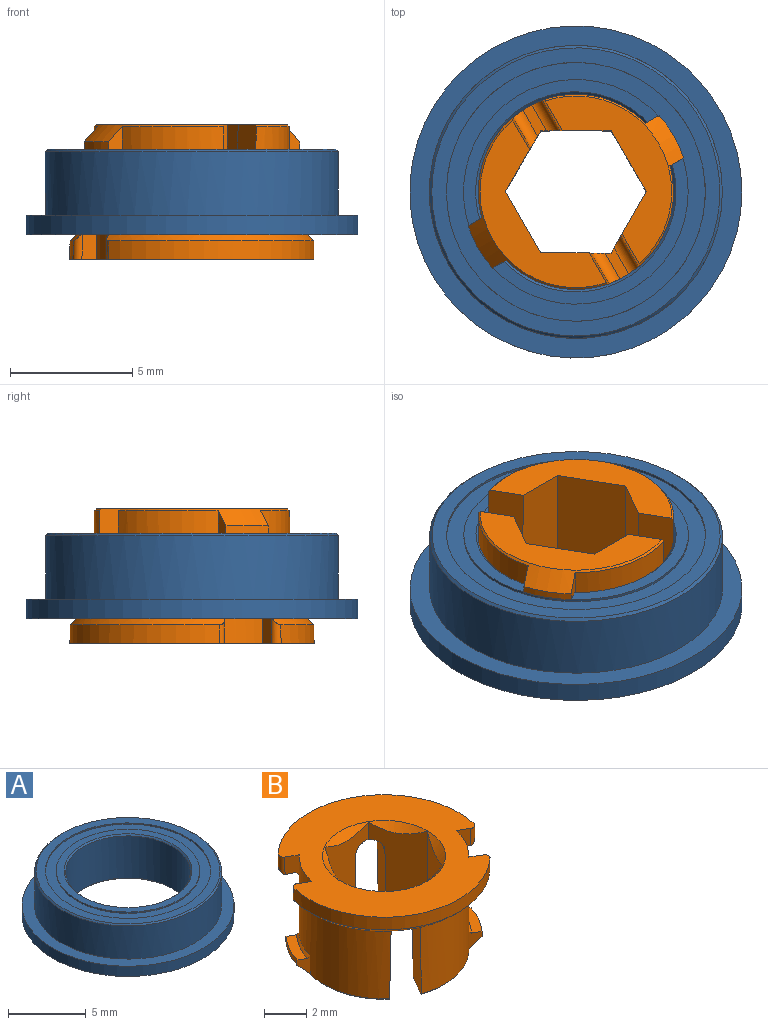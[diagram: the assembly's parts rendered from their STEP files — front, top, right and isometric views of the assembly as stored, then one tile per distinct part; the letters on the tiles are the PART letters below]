
ASSEMBLY  parts=2 mates=1
PART A: 17 faces, bbox 13.6x13.6x3.5 mm
  f0: plane 13.6x13.6mm, normal (0,0,-1), area 57mm2, adj f1,f2
  f1: cylinder r=5.3mm len=10.6mm, axis (0,0,1), area 3.3mm2, adj f0,f3
  f2: cylinder r=6.8mm len=13.6mm, axis (0,0,1), area 34.2mm2, adj f0,f4
  f3: plane 10.6x10.6mm, normal (0,0,-1), area 21.8mm2, adj f1,f5
  f4: plane 13.6x13.6mm, normal (0,0,1), area 32.2mm2, adj f2,f6
  f5: cylinder r=4.6mm len=9.2mm, axis (0,0,1), area 2.9mm2, adj f3,f7
  f6: cylinder r=6mm len=12mm, axis (0,0,1), area 98mm2, adj f4,f8
  f7: plane 9.2x9.2mm, normal (0,0,-1), area 13.7mm2, adj f5,f9
  f8: cone r=0mm half-angle=45deg, axis (0,0,-1), area 5.3mm2, adj f6,f10
  f9: cone r=0mm half-angle=45deg, axis (0,0,-1), area 3.6mm2, adj f7,f11
  f10: plane 11.8x11.8mm, normal (0,0,1), area 21.1mm2, adj f8,f12
  f11: cylinder r=4mm len=8mm, axis (0,0,1), area 82.9mm2, adj f9,f13
  f12: cylinder r=5.3mm len=10.6mm, axis (0,0,1), area 3.3mm2, adj f10,f14
  f13: cone r=0mm half-angle=45deg, axis (0,0,1), area 3.6mm2, adj f11,f15
  f14: plane 10.6x10.6mm, normal (0,0,1), area 21.8mm2, adj f12,f16
  f15: plane 9.2x9.2mm, normal (0,0,1), area 13.7mm2, adj f13,f16
  f16: cylinder r=4.6mm len=9.2mm, axis (0,0,1), area 2.9mm2, adj f14,f15
PART B: 50 faces, bbox 10.1x10.1x5.6 mm
  f0: plane 1.99x1.45mm, normal (0,0,1), area 1mm2, adj f1,f2,f3,f4
  f1: cylinder r=4.62mm len=1.73mm, axis (0,0,-1), area 0.6mm2, adj f0,f2,f3,f9
  f2: plane 1.06x0.57mm, normal (0.5,0.87,0), area 0.4mm2, adj f0,f1,f4,f9,f12
  f3: plane 1.06x0.57mm, normal (-0.5,-0.87,0), area 0.4mm2, adj f0,f1,f4,f9,f12
  f4: cone r=0mm half-angle=45deg, axis (0,0,-1), area 0.4mm2, adj f0,f2,f3,f12
  f5: cone r=0mm half-angle=45deg, axis (0,0,1), area 1mm2, adj f7,f12,f13,f20
  f6: cone r=0mm half-angle=45deg, axis (0,0,1), area 4.6mm2, adj f10,f14,f15,f20
  f7: cylinder r=0.5mm len=1.69mm, axis (-0.5,-0.87,0), area 1.1mm2, adj f5,f8,f12,f20,f21
  f8: plane 4.01x1.34mm, normal (-0.87,0.5,-0.02), area 5.9mm2, adj f7,f9,f12,f21,f23
  f9: cone r=0mm half-angle=45deg, axis (0,0,1), area 2.9mm2, adj f1,f2,f3,f8,f12,f23,f24
  f10: cylinder r=0.25mm len=1.01mm, axis (-0.02,0.01,1), area 0.4mm2, adj f6,f15,f17,f20,f33
  f11: cone r=0mm half-angle=1deg, axis (0,0,1), area 9.5mm2, adj f25,f30,f31,f33
  f12: cylinder r=4mm len=7.15mm, axis (0,0,-1), area 47.9mm2, adj f2,f3,f4,f5,f7,f8,f9,f13
  f13: plane 1.15x0.61mm, normal (-0.5,-0.87,0), area 0.7mm2, adj f5,f12,f14,f20,f33
  f14: cylinder r=0.25mm len=1.01mm, axis (-0.02,0.01,-1), area 0.4mm2, adj f6,f13,f15,f20,f33
  f15: cone r=0mm half-angle=1deg, axis (0,0,1), area 9.5mm2, adj f6,f10,f14,f33
  f16: plane 1.99x1.45mm, normal (0,0,1), area 1mm2, adj f19,f35,f36,f37
  f17: plane 1.15x0.61mm, normal (-0.5,-0.87,0), area 0.7mm2, adj f10,f18,f20,f33,f45
  f18: cone r=0mm half-angle=45deg, axis (0,0,1), area 1mm2, adj f17,f20,f22,f45
  f19: cone r=0mm half-angle=45deg, axis (0,0,-1), area 0.4mm2, adj f16,f35,f37,f45
  f20: plane 8.14x6.05mm, normal (0,0,-1), area 7.4mm2, adj f5,f6,f7,f10,f13,f14,f17,f18
  f21: plane 5.61x2.62mm, normal (-0.87,-0.5,0), area 11.3mm2, adj f7,f8,f20,f23,f32,f38,f43
  f22: cylinder r=0.5mm len=1.69mm, axis (0.5,0.87,0), area 1.1mm2, adj f18,f20,f38,f39,f45
  f23: plane 6.87x5.17mm, normal (0,0,-1), area 11.4mm2, adj f8,f9,f21,f24,f32,f40
  f24: plane 4.01x1.29mm, normal (-0.87,0.5,-0.02), area 5.9mm2, adj f9,f12,f23,f28,f40
  f25: cylinder r=0.25mm len=1.01mm, axis (0.02,-0.01,1), area 0.4mm2, adj f11,f26,f31,f33,f41
  f26: plane 1.15x0.61mm, normal (0.5,0.87,0), area 0.7mm2, adj f12,f25,f27,f33,f41
  f27: cone r=0mm half-angle=45deg, axis (0,0,1), area 1mm2, adj f12,f26,f28,f41
  f28: cylinder r=0.5mm len=1.69mm, axis (-0.5,-0.87,0), area 1.1mm2, adj f12,f24,f27,f40,f41
  f29: plane 1.15x0.61mm, normal (0.5,0.87,0), area 0.7mm2, adj f30,f33,f34,f41,f45
  f30: cylinder r=0.25mm len=1.01mm, axis (0.02,-0.01,-1), area 0.4mm2, adj f11,f29,f31,f33,f41
  f31: cone r=0mm half-angle=45deg, axis (0,0,1), area 4.6mm2, adj f11,f25,f30,f41
  f32: plane 5.49x2.5mm, normal (-0.87,0.5,0), area 15.1mm2, adj f21,f23,f40,f43
  f33: plane 10x10mm, normal (0,0,1), area 47.5mm2, adj f10,f11,f12,f13,f14,f15,f17,f25
  f34: cone r=0mm half-angle=45deg, axis (0,0,1), area 1mm2, adj f29,f41,f44,f45
  f35: plane 1.06x0.57mm, normal (-0.5,-0.87,0), area 0.4mm2, adj f16,f19,f36,f45,f46
  f36: cylinder r=4.62mm len=1.73mm, axis (0,0,-1), area 0.6mm2, adj f16,f35,f37,f46
  f37: plane 1.06x0.57mm, normal (0.5,0.87,0), area 0.4mm2, adj f16,f19,f36,f45,f46
  f38: plane 5.61x3.01mm, normal (0,-1,0), area 11.3mm2, adj f20,f21,f22,f39,f42,f43,f47
  f39: plane 4.01x1.29mm, normal (0.87,-0.5,-0.02), area 5.9mm2, adj f22,f38,f45,f46,f47
  f40: plane 5.6x3mm, normal (0,1,0), area 11.3mm2, adj f23,f24,f28,f32,f41,f43,f48
  f41: plane 8.14x6.05mm, normal (0,0,-1), area 7.4mm2, adj f25,f26,f27,f28,f29,f30,f31,f34
  f42: plane 5.49x2.5mm, normal (0.87,-0.5,0), area 15.1mm2, adj f38,f43,f47,f48
  f43: cone r=0mm half-angle=45deg, axis (0,0,1), area 6.7mm2, adj f21,f32,f33,f38,f40,f42,f48
  f44: cylinder r=0.5mm len=1.69mm, axis (0.5,0.87,0), area 1.1mm2, adj f34,f41,f45,f48,f49
  f45: cylinder r=4mm len=7.15mm, axis (0,0,-1), area 47.9mm2, adj f17,f18,f19,f22,f29,f33,f34,f35
  f46: cone r=0mm half-angle=45deg, axis (0,0,1), area 2.9mm2, adj f35,f36,f37,f39,f45,f47,f49
  f47: plane 6.87x5.17mm, normal (0,0,-1), area 11.4mm2, adj f38,f39,f42,f46,f48,f49
  f48: plane 5.6x2.62mm, normal (0.87,0.5,0), area 11.3mm2, adj f40,f41,f42,f43,f44,f47,f49
  f49: plane 4.01x1.34mm, normal (0.87,-0.5,-0.02), area 5.9mm2, adj f44,f45,f46,f47,f48
PLACE A at identity
PLACE B rot(axis=(1,0,0),180deg) t=(0,0,0.5)mm
MATE fastened B.f1 <-> A.f1  axis (0,0,1) through (0,0,-1.75)mm
